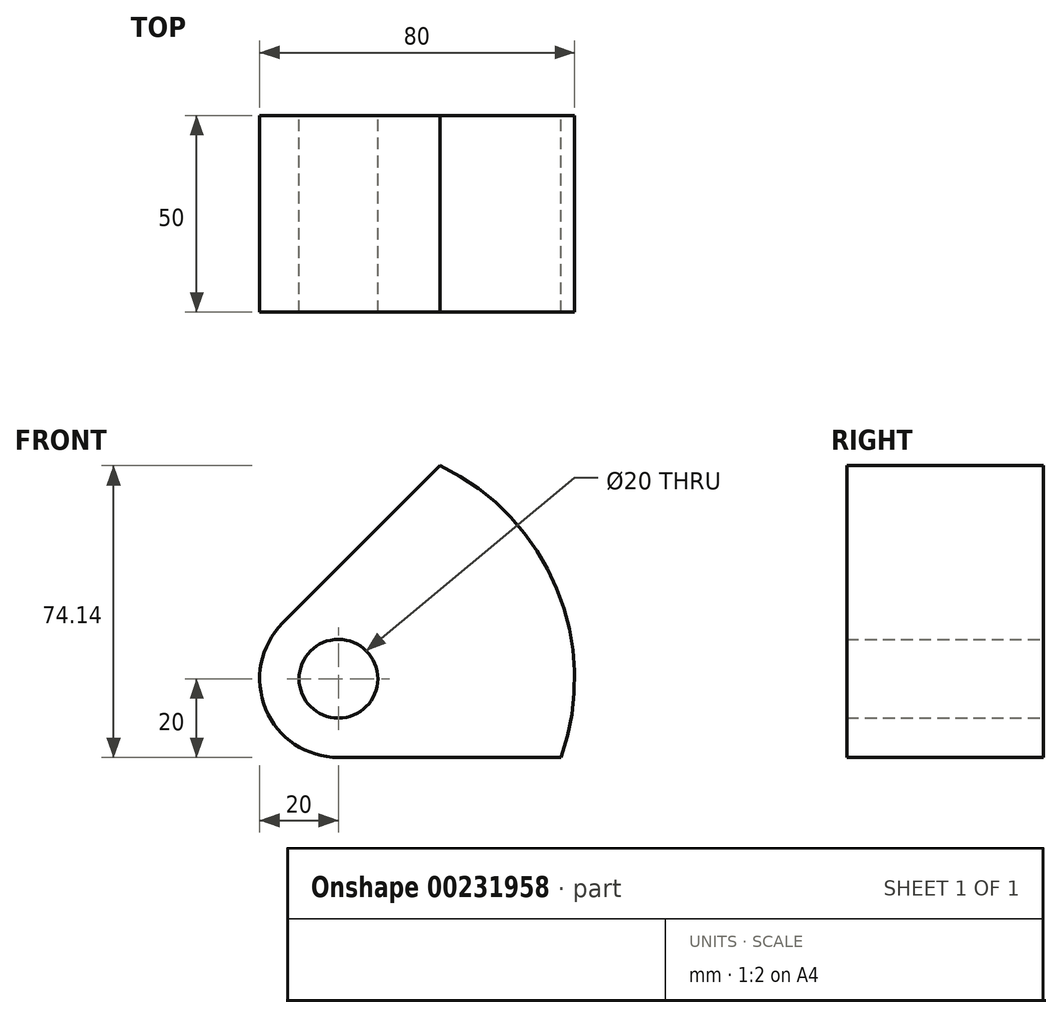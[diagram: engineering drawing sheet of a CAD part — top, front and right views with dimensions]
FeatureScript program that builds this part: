
annotation { "Feature Type Name" : "Feature", "Feature Type Description" : "" }
export const myFeature = defineFeature(function(context is Context, id is Id, definition is map)
    precondition{}
    {
        {
            var Q0;
            Q0=qCreatedBy(makeId("Front.planeOp"),FACE);
            var sketch = newSketch(context, id + "F0", { "sketchPlane" : qUnion([Q0])});
            skCircle(sketch, "E0", {"center": v(0, 0) * mm, "radius": 10 * mm});
            skArc(sketch, "E1", {"start": v(-14.14, 14.14) * mm, "mid": v(-18.48, -7.65) * mm, "end": v(0, -20) * mm});
            skLineSegment(sketch, "E2", {"start": v(0, -20) * mm, "end": v(56.57, -20) * mm});
            skLineSegment(sketch, "E3", {"start": v(-14.14, 14.14) * mm, "end": v(25.86, 54.14) * mm});
            skArc(sketch, "E4", {"start": v(56.57, -20) * mm, "mid": v(55.43, 22.96) * mm, "end": v(25.86, 54.14) * mm});
            skSolve(sketch);
        }
        {
            var Q0;
            Q0=makeQuery(id+"F0.imprint","IMPRINT",FACE,{"disambiguationData":[TD([[makeQuery(id+"F0.imprint","IMPRINT",EDGE,{"derivedFrom":sQuery(id+"F0.wireOp",EDGE,"E0")}),-1.0]])]});
            extrude(context, id + "F1", {"entities" : qUnion([Q0]), "endBound" : BoundingType.SYMMETRIC, "depth" : 50 * mm});
        }
    });
